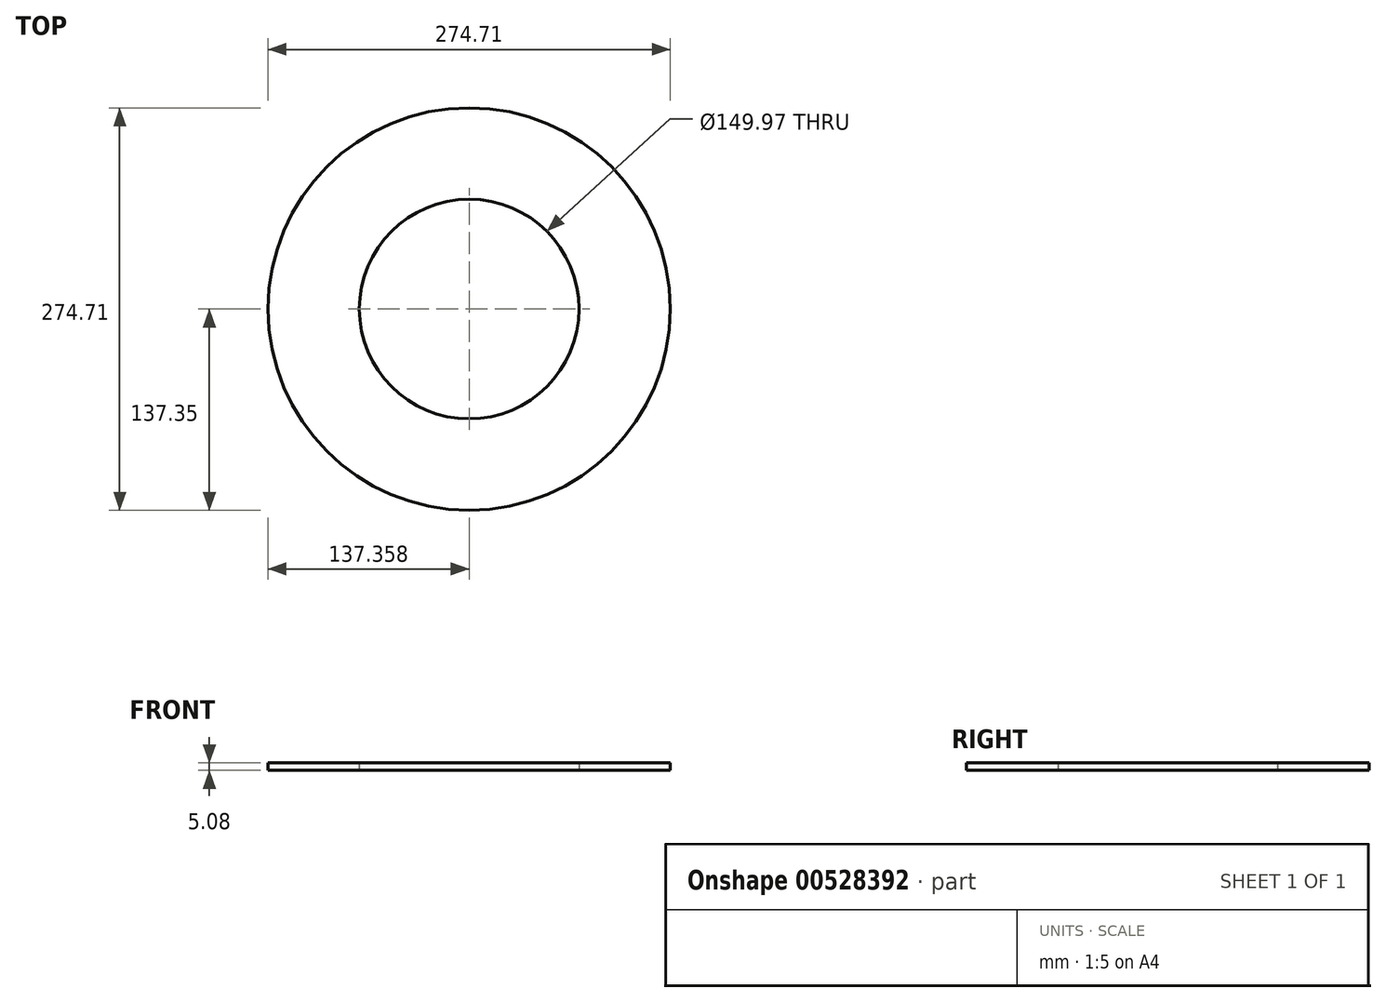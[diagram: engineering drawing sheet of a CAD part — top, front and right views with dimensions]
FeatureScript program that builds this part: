
annotation { "Feature Type Name" : "Feature", "Feature Type Description" : "" }
export const myFeature = defineFeature(function(context is Context, id is Id, definition is map)
    precondition{}
    {
        {
            var Q0;
            Q0=qCreatedBy(makeId("Top.planeOp"),FACE);
            var sketch = newSketch(context, id + "F0", { "sketchPlane" : qUnion([Q0])});
            skCircle(sketch, "E0", {"center": v(-16.72, -5.3) * mm, "radius": 137.36 * mm});
            skCircle(sketch, "E1", {"center": v(-16.72, -5.3) * mm, "radius": 74.98 * mm});
            skSolve(sketch);
        }
        {
            var Q0;
            Q0 = qSketchRegion(id + "F0", true);
            extrude(context, id + "F1", {"entities" : qUnion([Q0]), "depth" : 5.08 * mm, "offsetDistance" : 25.4 * mm});
        }
    });
